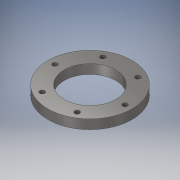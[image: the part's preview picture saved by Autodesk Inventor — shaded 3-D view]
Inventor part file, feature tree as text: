
AUTODESK INVENTOR PART (.ipt)
format: ipt  version: 2019 (Build 230136000, 136)  size: 123,904 bytes
history: native  units: in
note: dims shown in document units (in); Inventor stores cm internally (conversion verified against a paired STEP export)
features: sketch x2, extrude x1, hole x1
ambient origin geometry x8: Origin, YZ Plane, XZ Plane, XY Plane, X Axis, Y Axis, Z Axis, Center Point
bodies: Solid1 (feature_tree)
feature tree (4):
  extrude  "Extrusion1"  Depth=2.7559in
  hole  "Hole1"  [1 undecoded]
  sketch  "Sketch1"  dims[d0=4.5in d1=2.7559in]
  sketch  "Sketch2"  dims[d2=0.5in d3=0.0in d4=0.375in d5=2.3622in d7=360.0deg d9=0.257in d10=0.75in d11=0.438in d12=0.25in d13=0.5635in d14=0.484in d15=0.0in]
note: 1 required parameter value undecoded (feature->parameter linkage not recoverable at this tier; creation-order binding heuristic only, values carry confidence <= 0.55)
